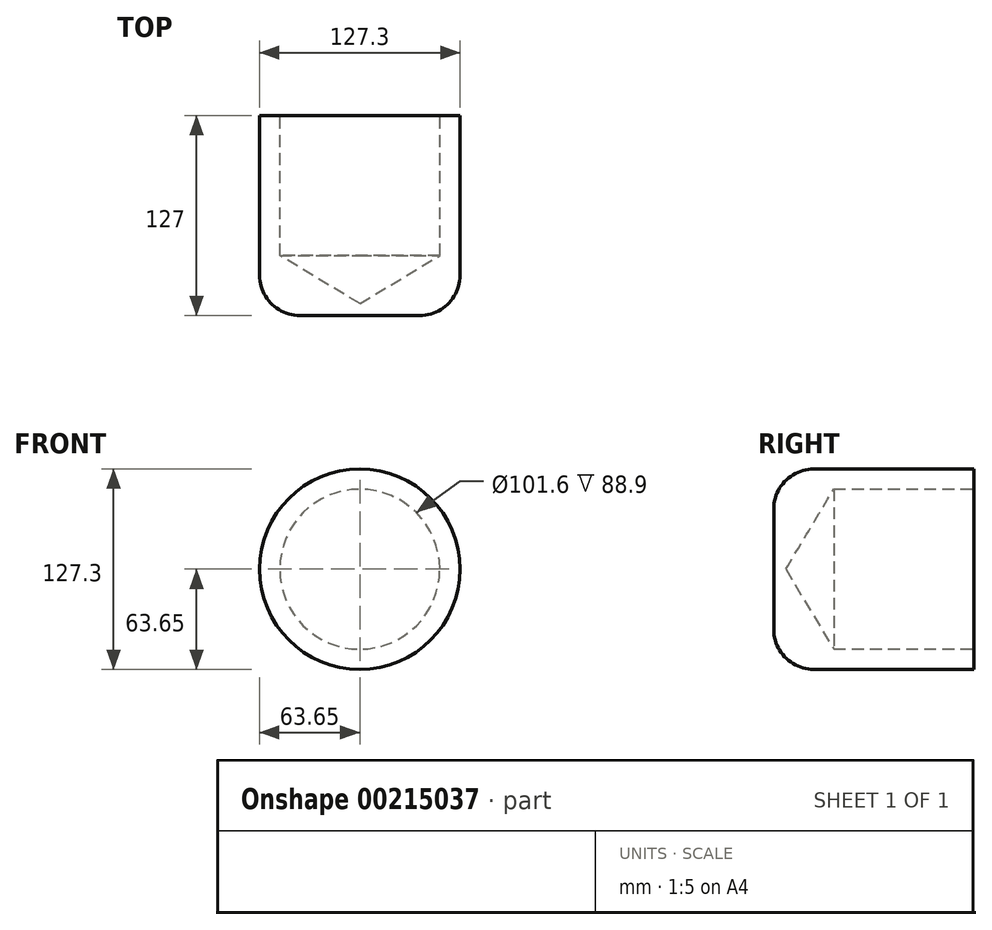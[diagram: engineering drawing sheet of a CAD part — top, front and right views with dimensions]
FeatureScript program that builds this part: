
annotation { "Feature Type Name" : "Feature", "Feature Type Description" : "" }
export const myFeature = defineFeature(function(context is Context, id is Id, definition is map)
    precondition{}
    {
        {
            var Q0;
            Q0=qCreatedBy(makeId("Front.planeOp"),FACE);
            var sketch = newSketch(context, id + "F0", { "sketchPlane" : qUnion([Q0])});
            skCircle(sketch, "E0", {"center": v(0, 0) * mm, "radius": 63.65 * mm});
            skSolve(sketch);
        }
        {
            var Q0;
            Q0 = qSketchRegion(id + "F0", true);
            extrude(context, id + "F1", {"entities" : qUnion([Q0]), "depth" : 127 * mm});
        }
        {
            var Q0;
            Q0=makeQuery(id+"F1.opExtrude","CAP_EDGE",EDGE,{"disambiguationData":[OSD([sQuery(id+"F0.wireOp",EDGE,"E0")])],"isStart":false});
            fillet(context, id + "F2", {"entities" : qUnion([Q0]), "radius" : 25.4 * mm, "tangentPropagation" : true, "allowEdgeOverflow" : false});
        }
        {
            var Q0;
            Q0=makeQuery(id+"F1.opExtrude","CAP_FACE",FACE,{"disambiguationData":[OSD([sQuery(id+"F0.wireOp",EDGE,"E0")])],"isStart":true});
            var sketch = newSketch(context, id + "F3", { "sketchPlane" : qUnion([Q0])});
            skCircle(sketch, "E1", {"center": v(0, 0) * mm, "radius": 50.72 * mm});
            skSolve(sketch);
        }
        {
            var Q0;
            Q0=sQuery(id+"F3.wireOp",VERTEX,"E1.center");
            var Q1;
            Q1=makeQuery(id+"F1.opExtrude","SWEPT_BODY",BODY,{"disambiguationData":[OSD([sQuery(id+"F0.wireOp",EDGE,"E0")])]});
            hole(context, id + "F4", {"style" : HoleStyle.SIMPLE, "endStyle" : HoleEndStyle.BLIND, "holeDiameter" : 101.6 * mm, "holeDepth" : 88.9 * mm, "locations" : qUnion([Q0]), "scope" : qUnion([Q1])});
        }
    });
